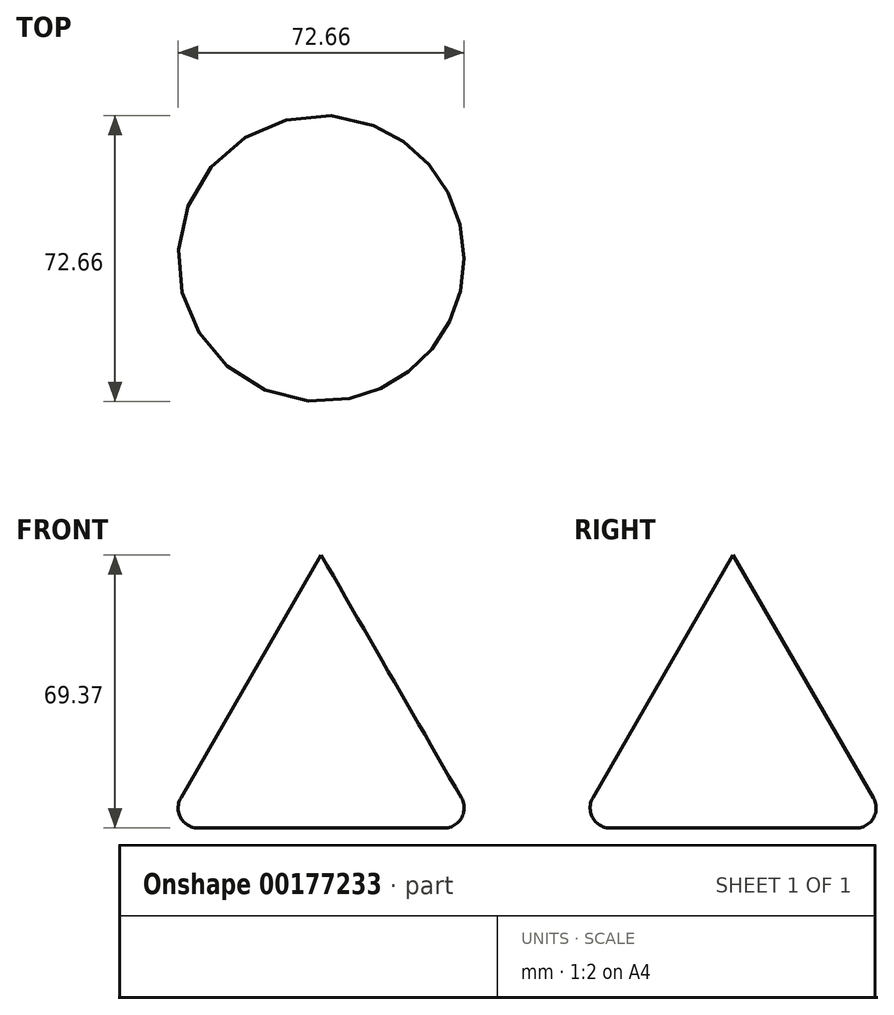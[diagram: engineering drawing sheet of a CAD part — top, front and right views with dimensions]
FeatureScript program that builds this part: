
annotation { "Feature Type Name" : "Feature", "Feature Type Description" : "" }
export const myFeature = defineFeature(function(context is Context, id is Id, definition is map)
    precondition{}
    {
        {
            var Q0;
            Q0=qCreatedBy(makeId("Top.planeOp"),FACE);
            var sketch = newSketch(context, id + "F0", { "sketchPlane" : qUnion([Q0])});
            skCircle(sketch, "E0", {"center": v(0, 0) * mm, "radius": 40.05 * mm});
            skSolve(sketch);
        }
        {
            var Q0;
            Q0=makeQuery(id+"F0.imprint","IMPRINT",FACE,{"disambiguationData":[TD([[makeQuery(id+"F0.imprint","IMPRINT",EDGE,{"derivedFrom":sQuery(id+"F0.wireOp",EDGE,"E0")}),1.0]])]});
            extrude(context, id + "F1", {"entities" : qUnion([Q0]), "depth" : 203.2 * mm, "hasDraft" : true, "draftAngle" : 30 * degree, "draftPullDirection" : true});
        }
        {
            var Q0;
            Q0=makeQuery(id+"F1.opExtrude","SWEPT_FACE",FACE,{"disambiguationData":[OSD([sQuery(id+"F0.wireOp",EDGE,"E0")])]});
            fillet(context, id + "F2", {"entities" : qUnion([Q0]), "radius" : 5.08 * mm, "tangentPropagation" : true, "allowEdgeOverflow" : false});
        }
    });
